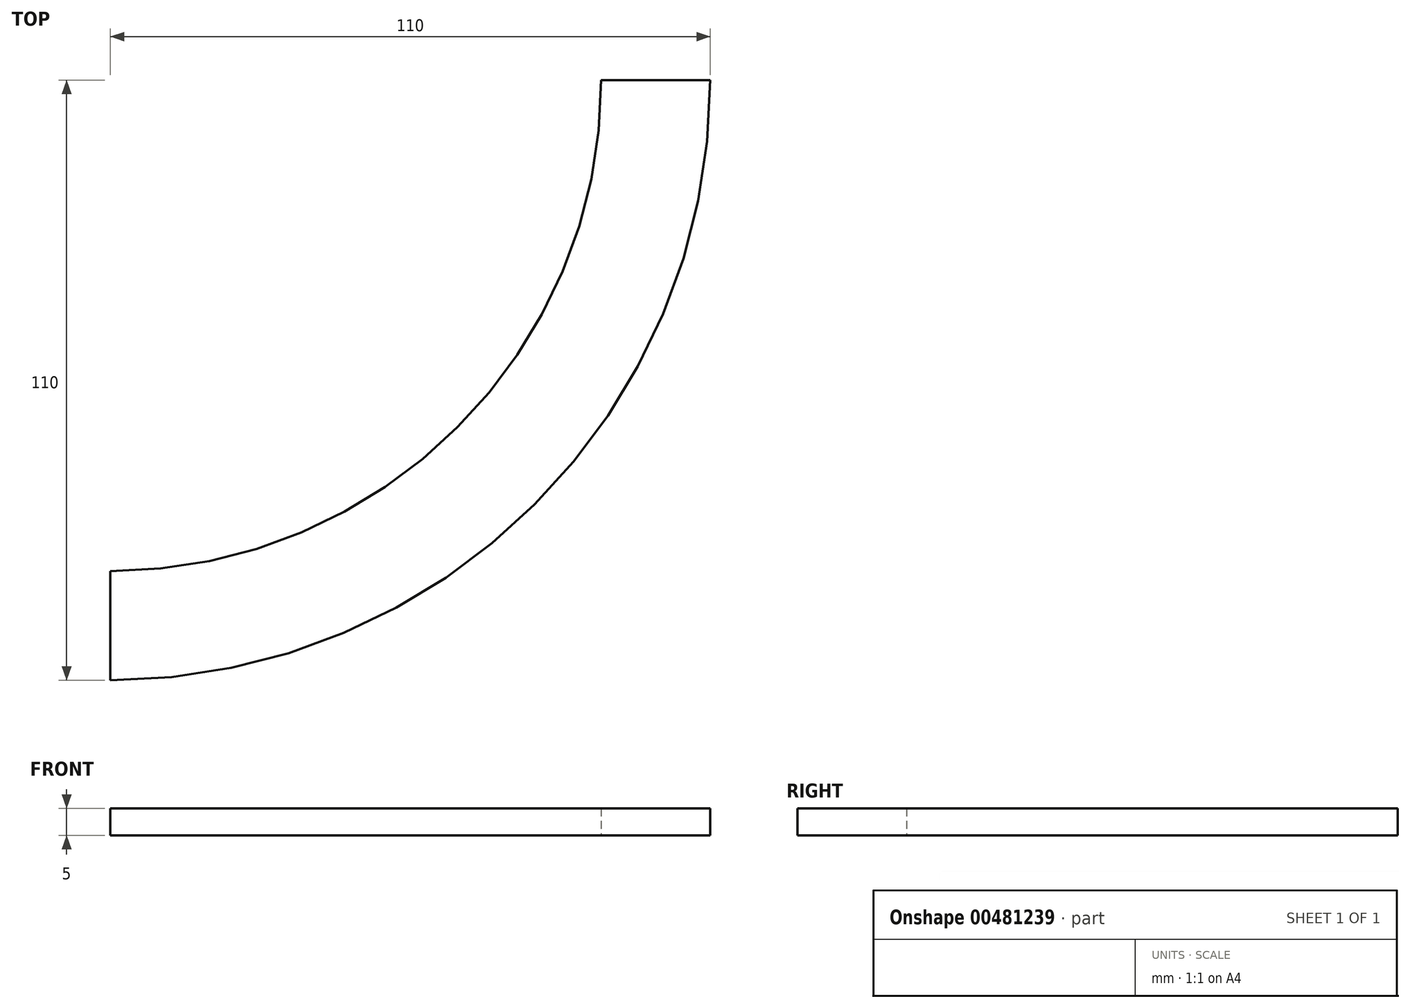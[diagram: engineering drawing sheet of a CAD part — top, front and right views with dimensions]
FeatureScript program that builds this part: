
annotation { "Feature Type Name" : "Feature", "Feature Type Description" : "" }
export const myFeature = defineFeature(function(context is Context, id is Id, definition is map)
    precondition{}
    {
        {
            var Q0;
            Q0=qCreatedBy(makeId("Top.planeOp"),FACE);
            var sketch = newSketch(context, id + "F0", { "sketchPlane" : qUnion([Q0])});
            skCircle(sketch, "E0", {"center": v(0, 0) * mm, "radius": 110 * mm});
            skCircle(sketch, "E1", {"center": v(0, 0) * mm, "radius": 90 * mm});
            skSolve(sketch);
        }
        {
            var Q0;
            Q0=makeQuery(id+"F0.imprint","IMPRINT",FACE,{"disambiguationData":[TD([[makeQuery(id+"F0.imprint","IMPRINT",EDGE,{"derivedFrom":sQuery(id+"F0.wireOp",EDGE,"E0")}),1.0]])]});
            extrude(context, id + "F1", {"entities" : qUnion([Q0]), "depth" : 5 * mm});
        }
        {
            var Q0;
            Q0=makeQuery(id+"F1.opExtrude","CAP_FACE",FACE,{"disambiguationData":[OSD([sQuery(id+"F0.wireOp",EDGE,"E0"),sQuery(id+"F0.wireOp",EDGE,"E1")])],"isStart":false});
            var sketch = newSketch(context, id + "F2", { "sketchPlane" : qUnion([Q0])});
            skCircle(sketch, "E2", {"center": v(0, 0) * mm, "radius": 100 * mm, "construction": true});
            skLineSegment(sketch, "E3", {"start": v(0, 0) * mm, "end": v(0, 135.06) * mm, "construction": true});
            skLineSegment(sketch, "E4", {"start": v(17.32, 100) * mm, "end": v(-17.32, 100) * mm, "construction": true});
            skLineSegment(sketch, "E5.top", {"start": v(-3.5, 95) * mm, "end": v(0, 95) * mm});
            skLineSegment(sketch, "E5.left", {"start": v(-3.5, 100) * mm, "end": v(-3.5, 95) * mm});
            skLineSegment(sketch, "E6.MirrorCS", {"start": v(3.5, 100) * mm, "end": v(3.5, 99.94) * mm});
            skLineSegment(sketch, "E7.MirrorCS", {"start": v(-3.5, 105) * mm, "end": v(0, 105) * mm});
            skLineSegment(sketch, "E8.MirrorCS", {"start": v(-3.5, 100) * mm, "end": v(-3.5, 105) * mm});
            skLineSegment(sketch, "E9.MirrorCS", {"start": v(3.5, 95) * mm, "end": v(0, 95) * mm});
            skLineSegment(sketch, "E10.MirrorCS", {"start": v(3.5, 100) * mm, "end": v(3.5, 95) * mm});
            skLineSegment(sketch, "E11.MirrorCS", {"start": v(3.5, 105) * mm, "end": v(0, 105) * mm});
            skLineSegment(sketch, "E12.MirrorCS", {"start": v(3.5, 100) * mm, "end": v(3.5, 105) * mm});
            skSolve(sketch);
        }
        {
            var Q0;
            Q0=makeQuery(id+"F1.opExtrude","CAP_FACE",FACE,{"disambiguationData":[OSD([sQuery(id+"F0.wireOp",EDGE,"E0"),sQuery(id+"F0.wireOp",EDGE,"E1")])],"isStart":false});
            var sketch = newSketch(context, id + "F3", { "sketchPlane" : qUnion([Q0])});
            skLineSegment(sketch, "E13", {"start": v(0, 0) * mm, "end": v(0, -124.39) * mm, "construction": true});
            skLineSegment(sketch, "E14", {"start": v(0, 0) * mm, "end": v(0, 128.62) * mm, "construction": true});
            skLineSegment(sketch, "E15", {"start": v(-17.32, 100) * mm, "end": v(17.32, 100) * mm, "construction": true});
            skCircle(sketch, "E16", {"center": v(0, 0) * mm, "radius": 100 * mm, "construction": true});
            skCircle(sketch, "E17", {"center": v(0, 0) * mm, "radius": 98.5 * mm});
            skCircle(sketch, "E18", {"center": v(0, 0) * mm, "radius": 101.5 * mm});
            skCircle(sketch, "E19", {"center": v(0, 0) * mm, "radius": 103 * mm});
            skCircle(sketch, "E20", {"center": v(0, 0) * mm, "radius": 106 * mm});
            skCircle(sketch, "E21", {"center": v(0, 0) * mm, "radius": 97 * mm});
            skCircle(sketch, "E22", {"center": v(0, 0) * mm, "radius": 94 * mm});
            skSolve(sketch);
        }
        {
            var Q0;
            Q0 = qSketchRegion(id + "F2", true);
            extrude(context, id + "F4", {"entities" : qUnion([Q0]), "operationType" : NewBodyOperationType.REMOVE, "oppositeDirection" : true, "depth" : 1 * mm});
        }
        {
            var Q0;
            Q0=qCreatedBy(makeId("Front.planeOp"),FACE);
            var sketch = newSketch(context, id + "F5", { "sketchPlane" : qUnion([Q0])});
            skLineSegment(sketch, "E23", {"start": v(0, 0) * mm, "end": v(0, -50) * mm, "construction": true});
            skSolve(sketch);
        }
        {
            var Q0;
            Q0=qCreatedBy(makeId("Right.planeOp"),FACE);
            var sketch = newSketch(context, id + "F6", { "sketchPlane" : qUnion([Q0])});
            skLineSegment(sketch, "E24.bottom", {"start": v(127.53, 22.31) * mm, "end": v(-125.34, 22.31) * mm});
            skLineSegment(sketch, "E24.top", {"start": v(127.53, -25.16) * mm, "end": v(-125.34, -25.16) * mm});
            skLineSegment(sketch, "E24.left", {"start": v(127.53, 22.31) * mm, "end": v(127.53, -25.16) * mm});
            skLineSegment(sketch, "E24.right", {"start": v(-125.34, 22.31) * mm, "end": v(-125.34, -25.16) * mm});
            skSolve(sketch);
        }
        {
            var Q0;
            Q0=makeQuery(id+"F6.imprint","IMPRINT",FACE,{"disambiguationData":[TD([[makeQuery(id+"F6.imprint","IMPRINT",EDGE,{"derivedFrom":sQuery(id+"F6.wireOp",EDGE,"E24.bottom")}),1.0]])]});
            extrude(context, id + "F7", {"entities" : qUnion([Q0]), "operationType" : NewBodyOperationType.REMOVE, "endBound" : BoundingType.THROUGH_ALL, "oppositeDirection" : true, "depth" : 25 * mm});
        }
        {
            var Q0;
            Q0=qCreatedBy(makeId("Front.planeOp"),FACE);
            var sketch = newSketch(context, id + "F8", { "sketchPlane" : qUnion([Q0])});
            skLineSegment(sketch, "E25.bottom", {"start": v(-109.4, 24.31) * mm, "end": v(121.67, 24.31) * mm});
            skLineSegment(sketch, "E25.top", {"start": v(-109.4, -17.7) * mm, "end": v(121.67, -17.7) * mm});
            skLineSegment(sketch, "E25.left", {"start": v(-109.4, 24.31) * mm, "end": v(-109.4, -17.7) * mm});
            skLineSegment(sketch, "E25.right", {"start": v(121.67, 24.31) * mm, "end": v(121.67, -17.7) * mm});
            skSolve(sketch);
        }
        {
            var Q0;
            Q0=makeQuery(id+"F8.imprint","IMPRINT",FACE,{"disambiguationData":[TD([[makeQuery(id+"F8.imprint","IMPRINT",EDGE,{"derivedFrom":sQuery(id+"F8.wireOp",EDGE,"E25.bottom")}),-1.0]])]});
            extrude(context, id + "F9", {"entities" : qUnion([Q0]), "operationType" : NewBodyOperationType.REMOVE, "endBound" : BoundingType.THROUGH_ALL, "oppositeDirection" : true, "depth" : 25 * mm});
        }
    });
